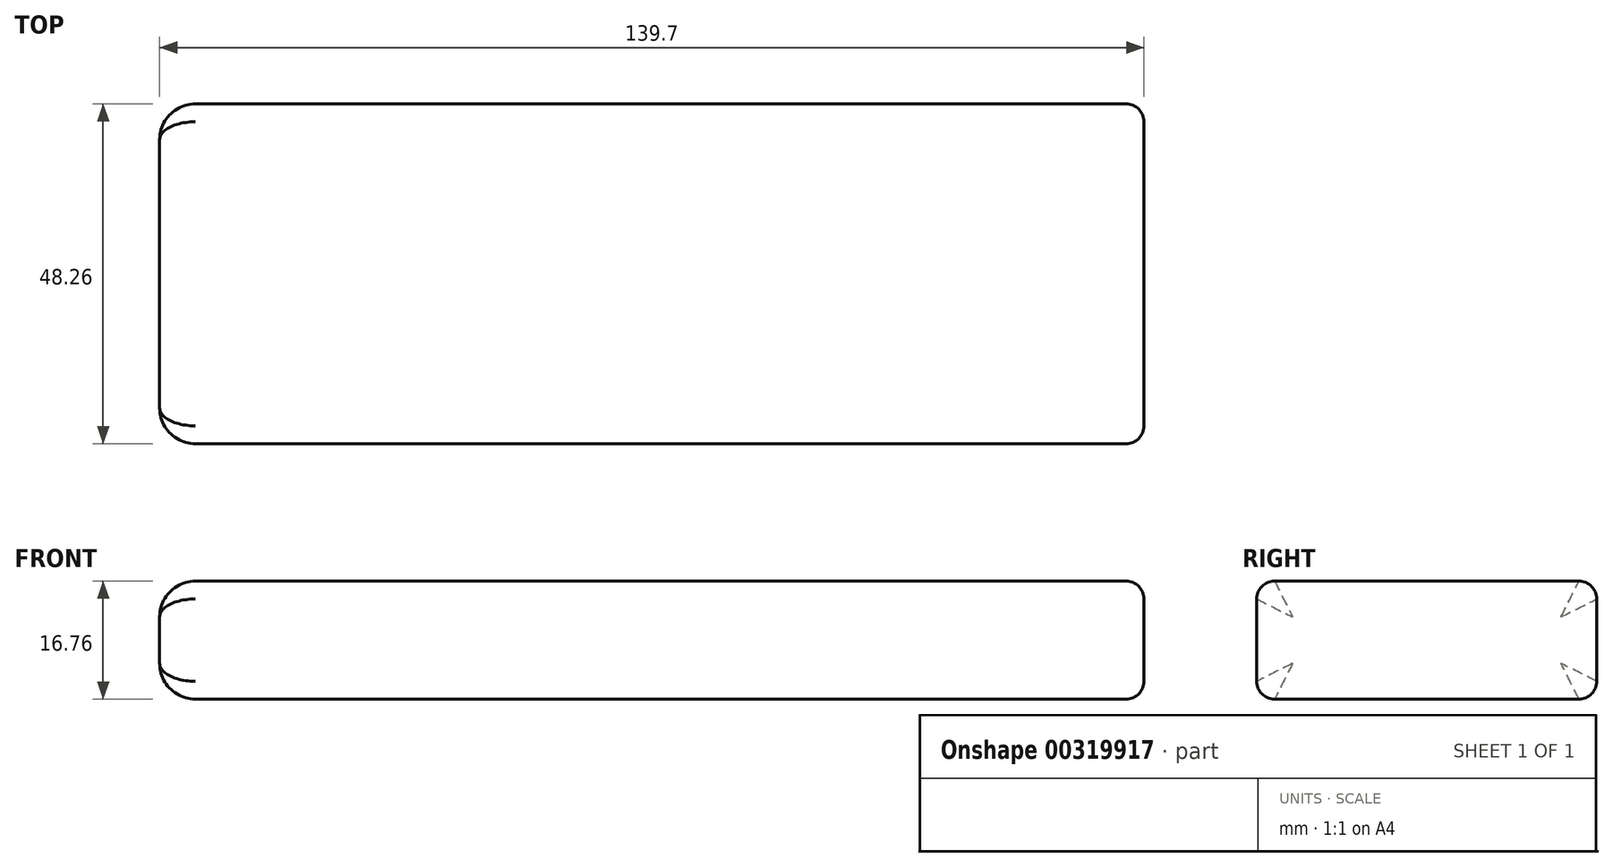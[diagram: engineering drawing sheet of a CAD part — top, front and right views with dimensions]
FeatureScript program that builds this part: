
annotation { "Feature Type Name" : "Feature", "Feature Type Description" : "" }
export const myFeature = defineFeature(function(context is Context, id is Id, definition is map)
    precondition{}
    {
        {
            var Q0;
            Q0=qCreatedBy(makeId("Top.planeOp"),FACE);
            var sketch = newSketch(context, id + "F0", { "sketchPlane" : qUnion([Q0])});
            skLineSegment(sketch, "E0.bottom", {"start": v(69.85, -24.13) * mm, "end": v(-69.85, -24.13) * mm});
            skLineSegment(sketch, "E0.top", {"start": v(69.85, 24.13) * mm, "end": v(-69.85, 24.13) * mm});
            skLineSegment(sketch, "E0.left", {"start": v(69.85, -24.13) * mm, "end": v(69.85, 24.13) * mm});
            skLineSegment(sketch, "E0.right", {"start": v(-69.85, -24.13) * mm, "end": v(-69.85, 24.13) * mm});
            skPoint(sketch, "E0.middle", {"position": v(0, 0) * mm});
            skSolve(sketch);
        }
        {
            var Q0;
            Q0=makeQuery(id+"F0.imprint","IMPRINT",FACE,{"disambiguationData":[TD([[makeQuery(id+"F0.imprint","IMPRINT",EDGE,{"derivedFrom":sQuery(id+"F0.wireOp",EDGE,"E0.bottom")}),-1.0]])]});
            extrude(context, id + "F1", {"entities" : qUnion([Q0]), "depth" : 16.76 * mm, "symmetric" : true});
        }
        {
            var Q0;
            Q0=makeQuery(id+"F1.opExtrude","CAP_EDGE",EDGE,{"disambiguationData":[OSD([sQuery(id+"F0.wireOp",EDGE,"E0.bottom")])],"isStart":false});
            var Q1;
            Q1=makeQuery(id+"F1.opExtrude","CAP_EDGE",EDGE,{"disambiguationData":[OSD([sQuery(id+"F0.wireOp",EDGE,"E0.top")])],"isStart":false});
            var Q2;
            Q2=makeQuery(id+"F1.opExtrude","CAP_EDGE",EDGE,{"disambiguationData":[OSD([sQuery(id+"F0.wireOp",EDGE,"E0.bottom")])],"isStart":true});
            var Q3;
            Q3=makeQuery(id+"F1.opExtrude","CAP_EDGE",EDGE,{"disambiguationData":[OSD([sQuery(id+"F0.wireOp",EDGE,"E0.top")])],"isStart":true});
            fillet(context, id + "F2", {"entities" : qUnion([Q0, Q1, Q2, Q3]), "radius" : 2.54 * mm, "tangentPropagation" : true, "allowEdgeOverflow" : false});
        }
        {
            var Q0;
            Q0=makeQuery(id+"F1.opExtrude","CAP_EDGE",EDGE,{"disambiguationData":[OSD([sQuery(id+"F0.wireOp",EDGE,"E0.right")])],"isStart":false});
            var Q1;
            Q1=makeQuery(id+"F1.opExtrude","CAP_EDGE",EDGE,{"disambiguationData":[OSD([sQuery(id+"F0.wireOp",EDGE,"E0.right")])],"isStart":true});
            fillet(context, id + "F3", {"entities" : qUnion([Q0, Q1]), "radius" : 5.08 * mm, "tangentPropagation" : true, "allowEdgeOverflow" : false});
        }
        {
            var Q0;
            Q0=makeQuery(id+"F1.opExtrude","CAP_EDGE",EDGE,{"disambiguationData":[OSD([sQuery(id+"F0.wireOp",EDGE,"E0.left")])],"isStart":false});
            fillet(context, id + "F4", {"entities" : qUnion([Q0]), "radius" : 2.54 * mm, "tangentPropagation" : true, "allowEdgeOverflow" : false});
        }
    });
